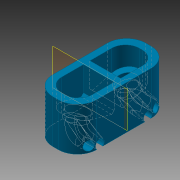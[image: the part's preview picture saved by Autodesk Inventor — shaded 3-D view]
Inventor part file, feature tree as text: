
AUTODESK INVENTOR PART (.ipt)
format: ipt  version: 2015 SP2 (Build 190223200, 223)  size: 380,416 bytes
history: native  units: in
note: dims shown in document units (in); Inventor stores cm internally (conversion verified against a paired STEP export)
features: sketch x5, extrude x4, mirror x3, plane x2, fillet x2, loft x2, revolve x1
ambient origin geometry x8: Origin, YZ Plane, XZ Plane, XY Plane, X Axis, Y Axis, Z Axis, Center Point
bodies: Solid1 (feature_tree)
feature tree (19):
  extrude  "Extrusion1"  TaperAngle=105.0deg  [1 undecoded]
  extrude  "Extrusion2"  Depth=0.28in TaperAngle=0.0deg
  plane  "Work Plane1"
  mirror  "Mirror1"
  plane  "Work Plane2"
  extrude  "Extrusion3"  Depth=0.18in
  mirror  "Mirror2"
  fillet  "Fillet4"  Radius=0.265in
  fillet  "Fillet5"  Radius=0.06in
  sketch  "Sketch4"  dims[d12=0.06in d13=0.0in d14=0.18in d15=0.265in d16=0.06in d17=0.0in]
  revolve  "Revolution1"  Angle=90.0deg
  extrude  "Extrusion7"  Depth=0.3957in
  sketch  "Sketch8"  dims[d33=0.15in d34=0.3957in d35=0.03in d36=0.07in d41=0.125in d42=0.175in d43=0.045in d44=0.08in d47=0.1in d48=1.0in d49=0.0in d50=0.0in d51=90.0deg d52=0.0in d53=90.0deg d54=0.0in d55=90.0deg d56=0.0in d57=90.0deg]
  loft  "Loft1"
  loft  "Loft2"
  mirror  "Mirror11"
  sketch  "Sketch2"  dims[d0=0.425in d1=105.0deg]
  sketch  "Sketch3"  dims[d8=0.03in d10=0.28in d11=0.0in]
  sketch  "Sketch7"  dims[d18=0.045in d20=90.0deg]
note: 1 required parameter value undecoded (feature->parameter linkage not recoverable at this tier; creation-order binding heuristic only, values carry confidence <= 0.55)
